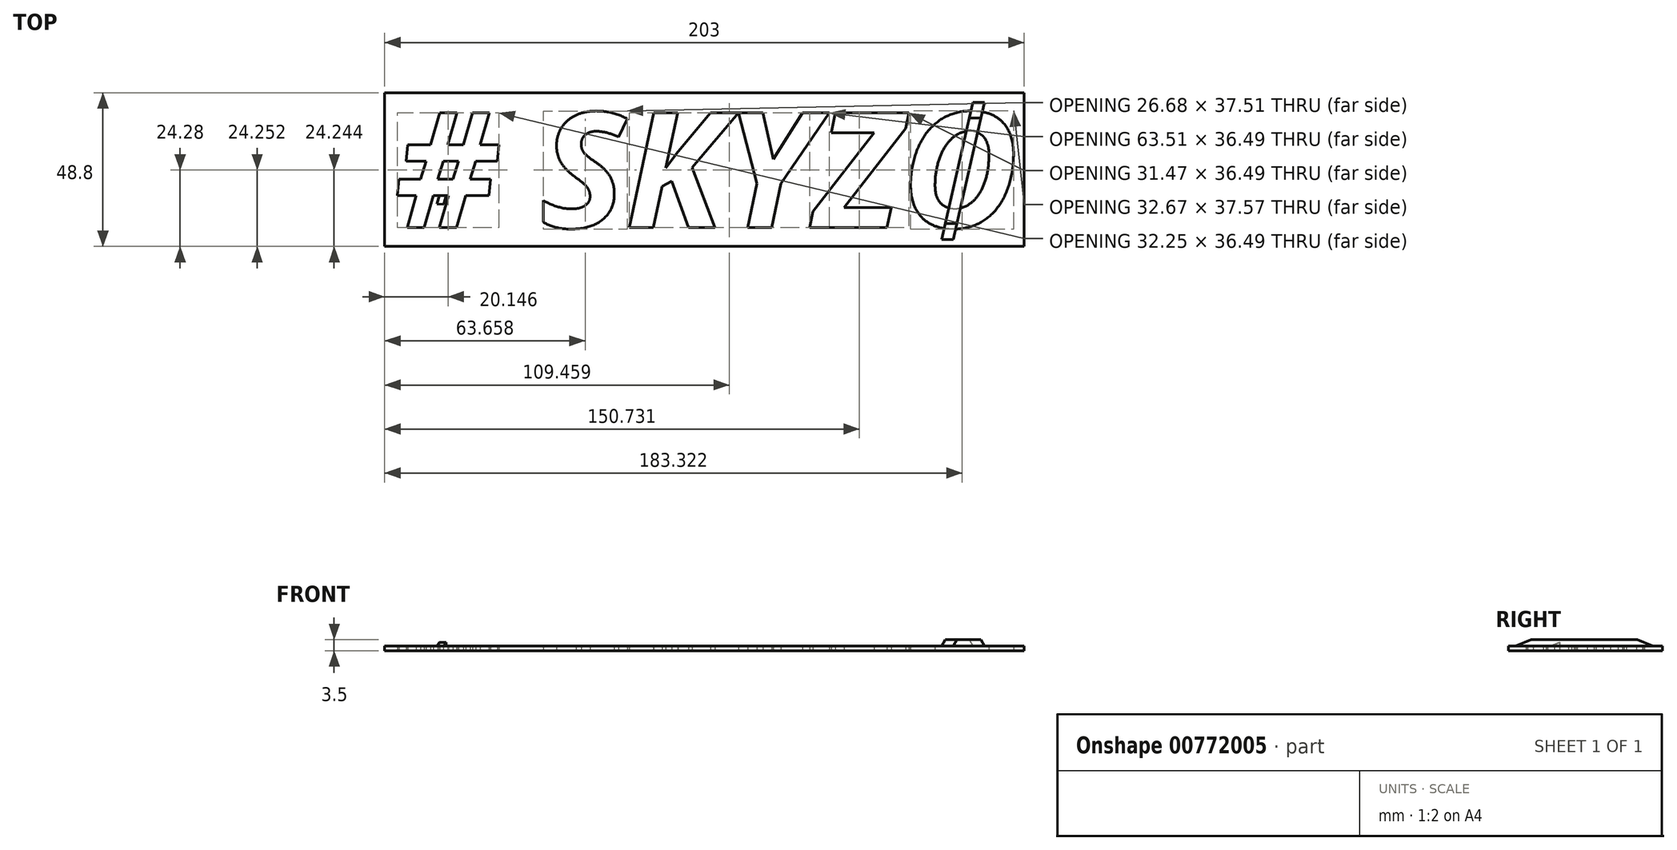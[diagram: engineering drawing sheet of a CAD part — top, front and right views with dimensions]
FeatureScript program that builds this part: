
annotation { "Feature Type Name" : "Feature", "Feature Type Description" : "" }
export const myFeature = defineFeature(function(context is Context, id is Id, definition is map)
    precondition{}
    {
        {
            var Q0;
            Q0=qCreatedBy(makeId("Top.planeOp"),FACE);
            var sketch = newSketch(context, id + "F0", { "sketchPlane" : qUnion([Q0])});
            skText(sketch, "E0", { "text": "# SKYZO", "fontName": "OpenSans-BoldItalic.ttf"});
            skLineSegment(sketch, "E1.bottom", {"start": v(-103, 22.98) * mm, "end": v(100, 22.98) * mm});
            skLineSegment(sketch, "E1.top", {"start": v(-103, -25.82) * mm, "end": v(100, -25.82) * mm});
            skLineSegment(sketch, "E1.left", {"start": v(-103, 22.98) * mm, "end": v(-103, -25.82) * mm});
            skLineSegment(sketch, "E1.right", {"start": v(100, 22.98) * mm, "end": v(100, -25.82) * mm});
            const initialGuessF0  = {"E0": [-0.1, -0.01982, 1, 0, 0.0368]};
            skSetInitialGuess(sketch, initialGuessF0);
            skSolve(sketch);
        }
        {
            var Q0;
            Q0=makeQuery(id+"F0.imprint","IMPRINT",FACE,{"disambiguationData":[TD([[makeQuery(id+"F0.imprint","IMPRINT",EDGE,{"derivedFrom":sQuery(id+"F0.wireOp",EDGE,"E0.sketch_text.stroke-0")}),1.0]])]});
            var Q1;
            Q1=makeQuery(id+"F0.imprint","IMPRINT",FACE,{"disambiguationData":[TD([[makeQuery(id+"F0.imprint","IMPRINT",EDGE,{"derivedFrom":sQuery(id+"F0.wireOp",EDGE,"E0.sketch_text.stroke-28")}),1.0]])]});
            var Q2;
            Q2=makeQuery(id+"F0.imprint","IMPRINT",FACE,{"disambiguationData":[TD([[makeQuery(id+"F0.imprint","IMPRINT",EDGE,{"derivedFrom":sQuery(id+"F0.wireOp",EDGE,"E0.sketch_text.stroke-98")}),1.0]])]});
            extrude(context, id + "F1", {"entities" : qUnion([Q0, Q1, Q2]), "depth" : 1.5 * mm, "offsetDistance" : 25 * mm});
        }
        {
            var Q0;
            Q0=makeQuery(id+"F1.opExtrude","CAP_FACE",FACE,{"disambiguationData":[OSD([sQuery(id+"F0.wireOp",EDGE,"E0.sketch_text.stroke-0"),sQuery(id+"F0.wireOp",EDGE,"E0.sketch_text.stroke-1"),sQuery(id+"F0.wireOp",EDGE,"E0.sketch_text.stroke-2"),sQuery(id+"F0.wireOp",EDGE,"E0.sketch_text.stroke-3"),sQuery(id+"F0.wireOp",EDGE,"E0.sketch_text.stroke-4"),sQuery(id+"F0.wireOp",EDGE,"E0.sketch_text.stroke-5"),sQuery(id+"F0.wireOp",EDGE,"E0.sketch_text.stroke-6"),sQuery(id+"F0.wireOp",EDGE,"E0.sketch_text.stroke-7"),sQuery(id+"F0.wireOp",EDGE,"E0.sketch_text.stroke-8"),sQuery(id+"F0.wireOp",EDGE,"E0.sketch_text.stroke-9"),sQuery(id+"F0.wireOp",EDGE,"E0.sketch_text.stroke-10"),sQuery(id+"F0.wireOp",EDGE,"E0.sketch_text.stroke-11"),sQuery(id+"F0.wireOp",EDGE,"E0.sketch_text.stroke-12"),sQuery(id+"F0.wireOp",EDGE,"E0.sketch_text.stroke-13"),sQuery(id+"F0.wireOp",EDGE,"E0.sketch_text.stroke-14"),sQuery(id+"F0.wireOp",EDGE,"E0.sketch_text.stroke-15"),sQuery(id+"F0.wireOp",EDGE,"E0.sketch_text.stroke-16"),sQuery(id+"F0.wireOp",EDGE,"E0.sketch_text.stroke-17"),sQuery(id+"F0.wireOp",EDGE,"E0.sketch_text.stroke-18"),sQuery(id+"F0.wireOp",EDGE,"E0.sketch_text.stroke-19"),sQuery(id+"F0.wireOp",EDGE,"E0.sketch_text.stroke-20"),sQuery(id+"F0.wireOp",EDGE,"E0.sketch_text.stroke-21"),sQuery(id+"F0.wireOp",EDGE,"E0.sketch_text.stroke-22"),sQuery(id+"F0.wireOp",EDGE,"E0.sketch_text.stroke-23"),sQuery(id+"F0.wireOp",EDGE,"E0.sketch_text.stroke-24"),sQuery(id+"F0.wireOp",EDGE,"E0.sketch_text.stroke-25"),sQuery(id+"F0.wireOp",EDGE,"E0.sketch_text.stroke-26"),sQuery(id+"F0.wireOp",EDGE,"E0.sketch_text.stroke-27"),sQuery(id+"F0.wireOp",EDGE,"E0.sketch_text.stroke-32"),sQuery(id+"F0.wireOp",EDGE,"E0.sketch_text.stroke-33"),sQuery(id+"F0.wireOp",EDGE,"E0.sketch_text.stroke-34"),sQuery(id+"F0.wireOp",EDGE,"E0.sketch_text.stroke-35"),sQuery(id+"F0.wireOp",EDGE,"E0.sketch_text.stroke-36"),sQuery(id+"F0.wireOp",EDGE,"E0.sketch_text.stroke-37"),sQuery(id+"F0.wireOp",EDGE,"E0.sketch_text.stroke-38"),sQuery(id+"F0.wireOp",EDGE,"E0.sketch_text.stroke-39"),sQuery(id+"F0.wireOp",EDGE,"E0.sketch_text.stroke-40"),sQuery(id+"F0.wireOp",EDGE,"E0.sketch_text.stroke-41"),sQuery(id+"F0.wireOp",EDGE,"E0.sketch_text.stroke-42"),sQuery(id+"F0.wireOp",EDGE,"E0.sketch_text.stroke-43"),sQuery(id+"F0.wireOp",EDGE,"E0.sketch_text.stroke-44"),sQuery(id+"F0.wireOp",EDGE,"E0.sketch_text.stroke-45"),sQuery(id+"F0.wireOp",EDGE,"E0.sketch_text.stroke-46"),sQuery(id+"F0.wireOp",EDGE,"E0.sketch_text.stroke-47"),sQuery(id+"F0.wireOp",EDGE,"E0.sketch_text.stroke-48"),sQuery(id+"F0.wireOp",EDGE,"E0.sketch_text.stroke-49"),sQuery(id+"F0.wireOp",EDGE,"E0.sketch_text.stroke-50"),sQuery(id+"F0.wireOp",EDGE,"E0.sketch_text.stroke-51"),sQuery(id+"F0.wireOp",EDGE,"E0.sketch_text.stroke-52"),sQuery(id+"F0.wireOp",EDGE,"E0.sketch_text.stroke-53"),sQuery(id+"F0.wireOp",EDGE,"E0.sketch_text.stroke-54"),sQuery(id+"F0.wireOp",EDGE,"E0.sketch_text.stroke-55"),sQuery(id+"F0.wireOp",EDGE,"E0.sketch_text.stroke-56"),sQuery(id+"F0.wireOp",EDGE,"E0.sketch_text.stroke-57"),sQuery(id+"F0.wireOp",EDGE,"E0.sketch_text.stroke-58"),sQuery(id+"F0.wireOp",EDGE,"E0.sketch_text.stroke-59"),sQuery(id+"F0.wireOp",EDGE,"E0.sketch_text.stroke-60"),sQuery(id+"F0.wireOp",EDGE,"E0.sketch_text.stroke-61"),sQuery(id+"F0.wireOp",EDGE,"E0.sketch_text.stroke-62"),sQuery(id+"F0.wireOp",EDGE,"E0.sketch_text.stroke-63"),sQuery(id+"F0.wireOp",EDGE,"E0.sketch_text.stroke-64"),sQuery(id+"F0.wireOp",EDGE,"E0.sketch_text.stroke-65"),sQuery(id+"F0.wireOp",EDGE,"E0.sketch_text.stroke-66"),sQuery(id+"F0.wireOp",EDGE,"E0.sketch_text.stroke-67"),sQuery(id+"F0.wireOp",EDGE,"E0.sketch_text.stroke-68"),sQuery(id+"F0.wireOp",EDGE,"E0.sketch_text.stroke-69"),sQuery(id+"F0.wireOp",EDGE,"E0.sketch_text.stroke-70"),sQuery(id+"F0.wireOp",EDGE,"E0.sketch_text.stroke-71"),sQuery(id+"F0.wireOp",EDGE,"E0.sketch_text.stroke-72"),sQuery(id+"F0.wireOp",EDGE,"E0.sketch_text.stroke-73"),sQuery(id+"F0.wireOp",EDGE,"E0.sketch_text.stroke-74"),sQuery(id+"F0.wireOp",EDGE,"E0.sketch_text.stroke-75"),sQuery(id+"F0.wireOp",EDGE,"E0.sketch_text.stroke-76"),sQuery(id+"F0.wireOp",EDGE,"E0.sketch_text.stroke-77"),sQuery(id+"F0.wireOp",EDGE,"E0.sketch_text.stroke-78"),sQuery(id+"F0.wireOp",EDGE,"E0.sketch_text.stroke-79"),sQuery(id+"F0.wireOp",EDGE,"E0.sketch_text.stroke-80"),sQuery(id+"F0.wireOp",EDGE,"E0.sketch_text.stroke-81"),sQuery(id+"F0.wireOp",EDGE,"E0.sketch_text.stroke-82"),sQuery(id+"F0.wireOp",EDGE,"E0.sketch_text.stroke-83"),sQuery(id+"F0.wireOp",EDGE,"E0.sketch_text.stroke-84"),sQuery(id+"F0.wireOp",EDGE,"E0.sketch_text.stroke-85"),sQuery(id+"F0.wireOp",EDGE,"E0.sketch_text.stroke-86"),sQuery(id+"F0.wireOp",EDGE,"E0.sketch_text.stroke-87"),sQuery(id+"F0.wireOp",EDGE,"E0.sketch_text.stroke-88"),sQuery(id+"F0.wireOp",EDGE,"E0.sketch_text.stroke-89"),sQuery(id+"F0.wireOp",EDGE,"E0.sketch_text.stroke-90"),sQuery(id+"F0.wireOp",EDGE,"E0.sketch_text.stroke-91"),sQuery(id+"F0.wireOp",EDGE,"E0.sketch_text.stroke-92"),sQuery(id+"F0.wireOp",EDGE,"E0.sketch_text.stroke-93"),sQuery(id+"F0.wireOp",EDGE,"E0.sketch_text.stroke-94"),sQuery(id+"F0.wireOp",EDGE,"E0.sketch_text.stroke-95"),sQuery(id+"F0.wireOp",EDGE,"E0.sketch_text.stroke-96"),sQuery(id+"F0.wireOp",EDGE,"E0.sketch_text.stroke-97"),sQuery(id+"F0.wireOp",EDGE,"E1.bottom"),sQuery(id+"F0.wireOp",EDGE,"E1.top"),sQuery(id+"F0.wireOp",EDGE,"E1.left"),sQuery(id+"F0.wireOp",EDGE,"E1.right")])],"isStart":false});
            var sketch = newSketch(context, id + "F2", { "sketchPlane" : qUnion([Q0])});
            skLineSegment(sketch, "E2", {"start": v(-80.84, 7.8) * mm, "end": v(-82.99, 0) * mm});
            skLineSegment(sketch, "E3", {"start": v(-82.99, 0) * mm, "end": v(-80.86, 0) * mm});
            skLineSegment(sketch, "E4", {"start": v(-80.86, 0) * mm, "end": v(-78.7, 7.8) * mm});
            skLineSegment(sketch, "E5", {"start": v(-78.7, 7.8) * mm, "end": v(-80.84, 7.8) * mm});
            skLineSegment(sketch, "E6", {"start": v(-80.84, 7.8) * mm, "end": v(-86.4, -12.36) * mm});
            skLineSegment(sketch, "E7", {"start": v(-78.7, 7.8) * mm, "end": v(-84.3, -12.5) * mm});
            skLineSegment(sketch, "E8", {"start": v(-86.4, -12.36) * mm, "end": v(-84.3, -12.5) * mm});
            skLineSegment(sketch, "E9", {"start": v(83.75, 19.97) * mm, "end": v(73.86, -23.6) * mm});
            skLineSegment(sketch, "E10", {"start": v(73.86, -23.6) * mm, "end": v(77.56, -23.6) * mm});
            skLineSegment(sketch, "E11", {"start": v(77.56, -23.6) * mm, "end": v(87.45, 19.97) * mm});
            skLineSegment(sketch, "E12", {"start": v(87.45, 19.97) * mm, "end": v(83.75, 19.97) * mm});
            skSolve(sketch);
        }
        {
            var Q0;
            {var subQ0=sQuery(id+"F2.wireOp",EDGE,"E3");Q0=makeQuery(id+"F2.imprint","IMPRINT",FACE,{"disambiguationData":[TD([[makeQuery(id+"F2.imprint","IMPRINT",EDGE,{"derivedFrom":subQ0}),1.0]])]});}
            var Q1;
            {var subQ0=sQuery(id+"F2.wireOp",EDGE,"E3");Q1=makeQuery(id+"F2.imprint","IMPRINT",FACE,{"disambiguationData":[TD([[makeQuery(id+"F2.imprint","IMPRINT",EDGE,{"derivedFrom":subQ0}),-1.0]])]});}
            var Q2;
            {var subQ0=sQuery(id+"F2.wireOp",EDGE,"E8");Q2=makeQuery(id+"F2.imprint","IMPRINT",FACE,{"disambiguationData":[TD([[makeQuery(id+"F2.imprint","IMPRINT",EDGE,{"derivedFrom":subQ0}),1.0]])]});}
            var Q3;
            {var subQ3=sQuery(id+"F2.wireOp",EDGE,"E9");var subQ9=makeQuery(id+"F1.opExtrude","CAP_EDGE",EDGE,{"disambiguationData":[OSD([sQuery(id+"F0.wireOp",EDGE,"E0.sketch_text.stroke-95")])],"isStart":false});var subQ10=makeQuery(id+"F2.imprint","INTERSECT",VERTEX,{"derivedFrom":[subQ9,subQ3]});Q3=makeQuery(id+"F2.imprint","IMPRINT",FACE,{"disambiguationData":[TD([[makeQuery(id+"F2.imprint","IMPRINT",EDGE,{"disambiguationData":[TD([[subQ10,-1.0]])],"derivedFrom":subQ3}),1.0]])]});}
            var Q4;
            {var subQ5=sQuery(id+"F2.wireOp",EDGE,"E10");Q4=makeQuery(id+"F2.imprint","IMPRINT",FACE,{"disambiguationData":[TD([[makeQuery(id+"F2.imprint","IMPRINT",EDGE,{"derivedFrom":subQ5}),1.0]])]});}
            var Q5;
            {var subQ0=sQuery(id+"F2.wireOp",EDGE,"E12");Q5=makeQuery(id+"F2.imprint","IMPRINT",FACE,{"disambiguationData":[TD([[makeQuery(id+"F2.imprint","IMPRINT",EDGE,{"derivedFrom":subQ0}),1.0]])]});}
            var Q6;
            {var subQ0=sQuery(id+"F2.wireOp",EDGE,"E5");Q6=makeQuery(id+"F2.imprint","IMPRINT",FACE,{"disambiguationData":[TD([[makeQuery(id+"F2.imprint","IMPRINT",EDGE,{"derivedFrom":subQ0}),1.0]])]});}
            extrude(context, id + "F3", {"entities" : qUnion([Q0, Q1, Q2, Q3, Q4, Q5, Q6]), "depth" : 2 * mm, "offsetDistance" : 25 * mm});
        }
        {
            var Q0;
            Q0=makeQuery(id+"F3.opExtrude","CAP_EDGE",EDGE,{"disambiguationData":[OSD([sQuery(id+"F2.wireOp",EDGE,"E5")])],"isStart":false});
            var Q1;
            Q1=makeQuery(id+"F3.opExtrude","CAP_EDGE",EDGE,{"disambiguationData":[OSD([sQuery(id+"F2.wireOp",EDGE,"E8")])],"isStart":false});
            var Q2;
            Q2=makeQuery(id+"F3.opExtrude","CAP_EDGE",EDGE,{"disambiguationData":[OSD([sQuery(id+"F2.wireOp",EDGE,"E10")])],"isStart":false});
            var Q3;
            Q3=makeQuery(id+"F3.opExtrude","CAP_EDGE",EDGE,{"disambiguationData":[OSD([sQuery(id+"F2.wireOp",EDGE,"E12")])],"isStart":false});
            chamfer(context, id + "F4", {"entities" : qUnion([Q0, Q1, Q2, Q3]), "chamferType" : ChamferType.TWO_OFFSETS, "width1" : 5 * mm, "oppositeDirection" : false, "width2" : 2 * mm, "tangentPropagation" : true});
        }
    });
